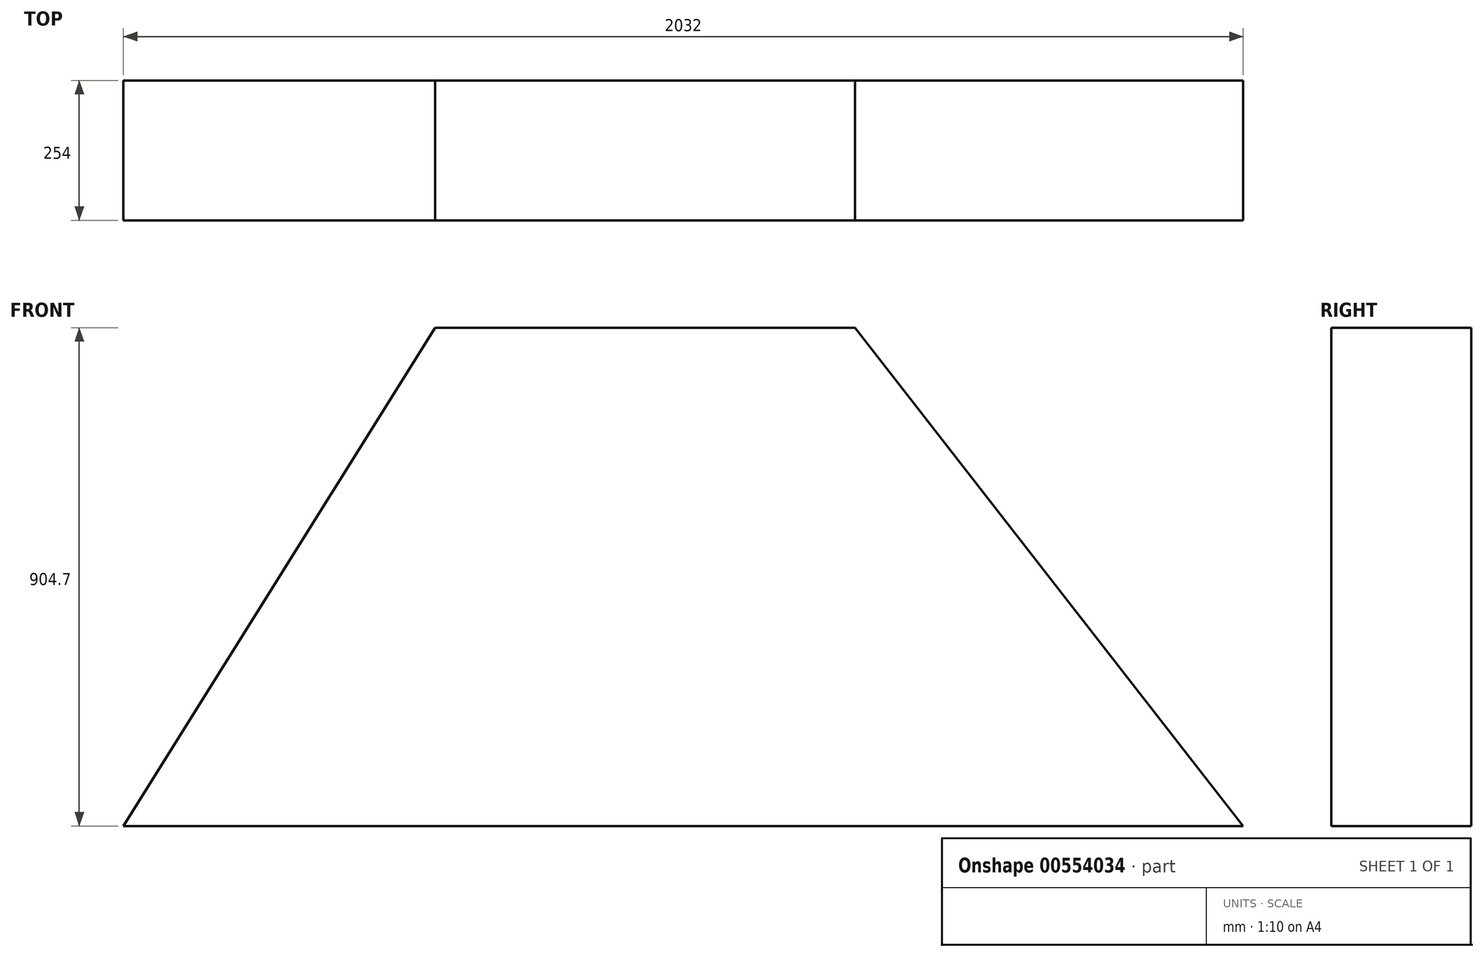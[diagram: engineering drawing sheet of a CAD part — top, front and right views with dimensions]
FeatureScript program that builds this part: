
annotation { "Feature Type Name" : "Feature", "Feature Type Description" : "" }
export const myFeature = defineFeature(function(context is Context, id is Id, definition is map)
    precondition{}
    {
        {
            var Q0;
            Q0=qCreatedBy(makeId("Front.planeOp"),FACE);
            var sketch = newSketch(context, id + "F0", { "sketchPlane" : qUnion([Q0])});
            skLineSegment(sketch, "E0", {"start": v(0, 0) * mm, "end": v(762, 0) * mm});
            skLineSegment(sketch, "E1", {"start": v(762, 0) * mm, "end": v(1466.68, -904.7) * mm});
            skLineSegment(sketch, "E2", {"start": v(0, 0) * mm, "end": v(-565.32, -904.7) * mm});
            skLineSegment(sketch, "E3", {"start": v(-565.32, -904.7) * mm, "end": v(1466.68, -904.7) * mm});
            skSolve(sketch);
        }
        {
            var Q0;
            Q0 = qSketchRegion(id + "F0", true);
            extrude(context, id + "F1", {"entities" : qUnion([Q0]), "depth" : 254 * mm, "offsetDistance" : 25.4 * mm});
        }
    });
